# Revit family: Haworth_MangasOriginal_Pouf_Globo
name_source: partatom
category: Furniture
revit_build: Autodesk Revit 2018 (Build: 20170223_1515(x64)
units: mm (PartAtom-declared; Revit-internal decimal feet)

## family parameters
Always vertical = Yes
Cut with Voids When Loaded = No
OmniClass Number = 23.35.50.27.11.11
OmniClass Title = Access Floors, Frames
Room Calculation Point = No
Shared = No
Work Plane-Based = No

## types (1)
- HCGN-MOFG - Globo Pouf
    Actual Depth = 39 1/2"
    Actual Height = 17"
    Actual Width = 35 1/2"
    Assembly Code = E2020200
    Description = Haworth - Mangas Original - Globo Pouf
    Manufacturer = Haworth
    Model = HCGN-MOFG
    Note = Verify Final Dimensions w/ Haworth
    Revision Number = 1
    Seat Finish Inner = Haworth _ Wool _ Mangas Original
    URL = http://www.haworth.com
    URL - Product = https://www.haworth.com
    Warranty = http://www.haworth.com

## geometry (parser evidence)
native form markers: Sweep x2
no freeform markers — native parametric forms only
